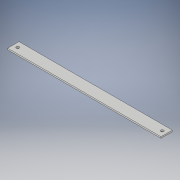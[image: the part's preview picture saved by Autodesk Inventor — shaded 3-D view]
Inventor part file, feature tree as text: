
AUTODESK INVENTOR PART (.ipt)
format: ipt  version: 2017 (Build 210142000, 142)  size: 103,936 bytes
history: native  units: in
note: dims shown in document units (in); Inventor stores cm internally (conversion verified against a paired STEP export)
features: extrude x2, sketch x2
ambient origin geometry x8: Origin, YZ Plane, XZ Plane, XY Plane, X Axis, Y Axis, Z Axis, Center Point
bodies: Solid1 (feature_tree)
feature tree (4):
  extrude  "Extrusion1"  Depth=1.0in
  extrude  "Extrusion2"  Depth=13.5in
  sketch  "Sketch1"  dims[d0=0.128in d1=1.0in]
  sketch  "Sketch2"  dims[d2=13.5in d3=0.0in d4=0.25in d5=6.364in d6=13.5in d7=0.0in]
